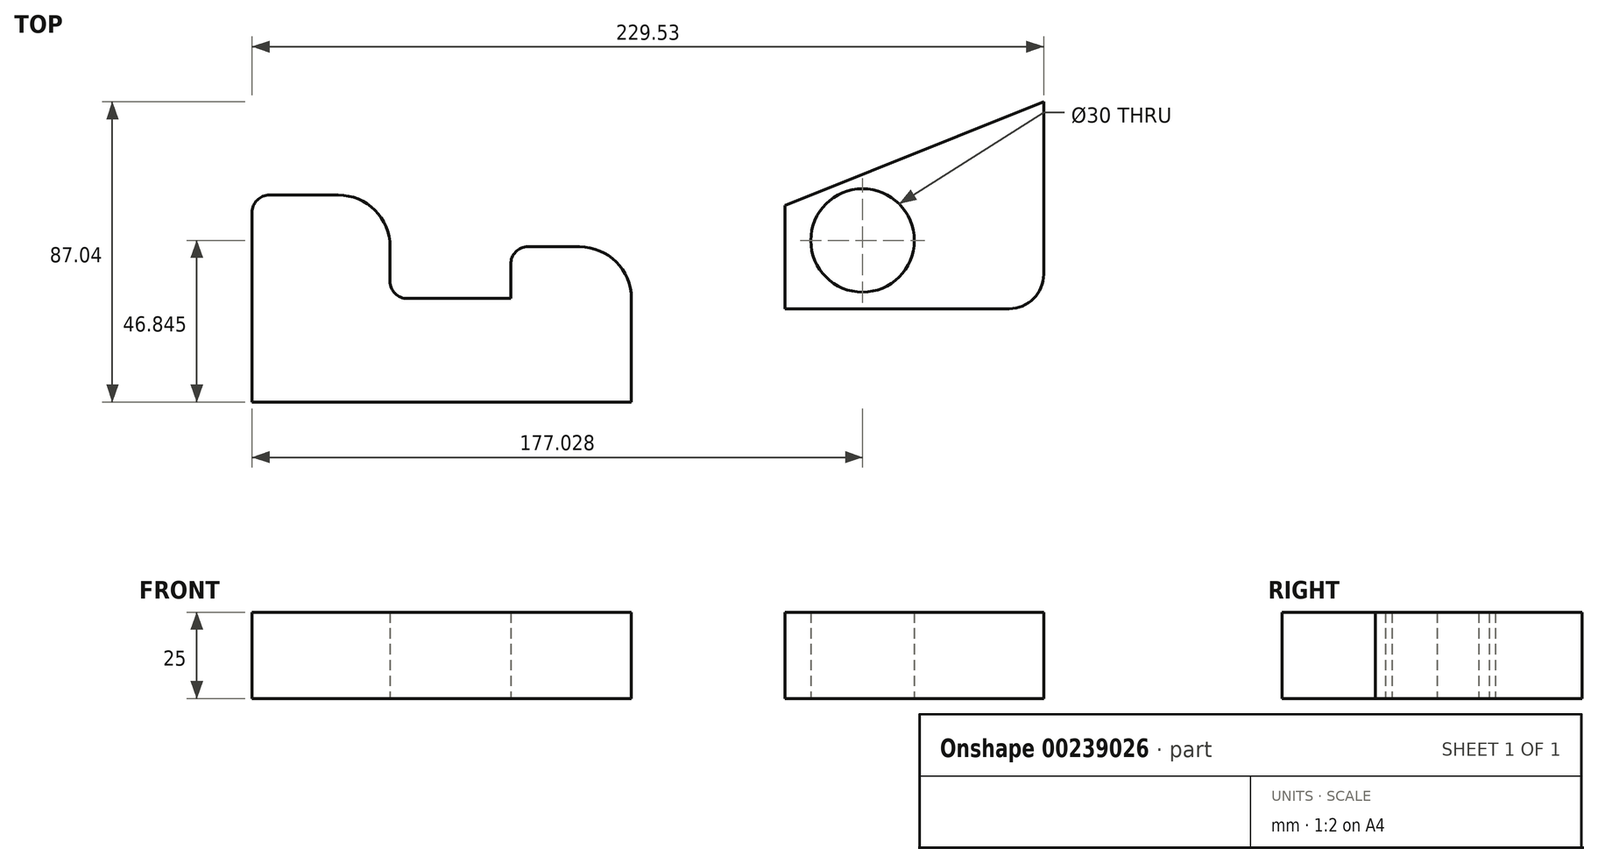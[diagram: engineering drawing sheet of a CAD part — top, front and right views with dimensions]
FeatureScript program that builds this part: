
annotation { "Feature Type Name" : "Feature", "Feature Type Description" : "" }
export const myFeature = defineFeature(function(context is Context, id is Id, definition is map)
    precondition{}
    {
        {
            var Q0;
            Q0=qCreatedBy(makeId("Top.planeOp"),FACE);
            var sketch = newSketch(context, id + "F0", { "sketchPlane" : qUnion([Q0])});
            skLineSegment(sketch, "E0", {"start": v(-99.18, -45) * mm, "end": v(10.82, -45) * mm});
            skLineSegment(sketch, "E1", {"start": v(-99.18, -45) * mm, "end": v(-99.18, 10) * mm});
            skLineSegment(sketch, "E2", {"start": v(-94.18, 15) * mm, "end": v(-74.18, 15) * mm});
            skPoint(sketch, "E3.visualSharp", {"position": v(-99.18, 15) * mm});
            skArc(sketch, "E3.filletArc", {"start": v(-94.18, 15) * mm, "mid": v(-97.72, 13.54) * mm, "end": v(-99.18, 10) * mm});
            skLineSegment(sketch, "E4", {"start": v(-59.18, 0) * mm, "end": v(-59.18, -10) * mm});
            skPoint(sketch, "E5.visualSharp", {"position": v(-59.18, 15) * mm});
            skArc(sketch, "E5.filletArc", {"start": v(-59.18, 0) * mm, "mid": v(-63.57, 10.6) * mm, "end": v(-74.18, 15) * mm});
            skLineSegment(sketch, "E6", {"start": v(-54.18, -15) * mm, "end": v(-24.18, -15) * mm});
            skPoint(sketch, "E7.visualSharp", {"position": v(-59.18, -15) * mm});
            skArc(sketch, "E7.filletArc", {"start": v(-59.18, -10) * mm, "mid": v(-57.72, -13.54) * mm, "end": v(-54.18, -15) * mm});
            skLineSegment(sketch, "E8", {"start": v(-24.18, -15) * mm, "end": v(-24.18, -5) * mm});
            skLineSegment(sketch, "E9", {"start": v(-19.18, 0) * mm, "end": v(-4.18, 0) * mm});
            skPoint(sketch, "E10.visualSharp", {"position": v(-24.18, 0) * mm});
            skArc(sketch, "E10.filletArc", {"start": v(-19.18, 0) * mm, "mid": v(-22.72, -1.46) * mm, "end": v(-24.18, -5) * mm});
            skLineSegment(sketch, "E11", {"start": v(10.82, -15) * mm, "end": v(10.82, -45) * mm});
            skLineSegment(sketch, "E12", {"start": v(10.82, -45) * mm, "end": v(10.82, -27.29) * mm});
            skPoint(sketch, "E13.visualSharp", {"position": v(10.82, 0) * mm});
            skArc(sketch, "E13.filletArc", {"start": v(10.82, -15) * mm, "mid": v(6.43, -4.4) * mm, "end": v(-4.18, 0) * mm});
            skLineSegment(sketch, "E14", {"start": v(55.35, -17.96) * mm, "end": v(120.35, -17.96) * mm});
            skLineSegment(sketch, "E15", {"start": v(130.35, -7.96) * mm, "end": v(130.35, 42.04) * mm});
            skLineSegment(sketch, "E16", {"start": v(55.35, -17.96) * mm, "end": v(55.35, 12.04) * mm});
            skLineSegment(sketch, "E17", {"start": v(55.35, 12.04) * mm, "end": v(130.35, 42.04) * mm});
            skPoint(sketch, "E18.visualSharp", {"position": v(130.35, -17.96) * mm});
            skArc(sketch, "E18.filletArc", {"start": v(120.35, -17.96) * mm, "mid": v(127.42, -15.04) * mm, "end": v(130.35, -7.96) * mm});
            skLineSegment(sketch, "E19", {"start": v(55.35, -17.96) * mm, "end": v(77.85, -17.96) * mm});
            skLineSegment(sketch, "E20", {"start": v(55.35, 12.04) * mm, "end": v(55.35, 1.84) * mm});
            skLineSegment(sketch, "E21", {"start": v(55.35, 1.84) * mm, "end": v(77.85, 1.84) * mm});
            skCircle(sketch, "E22", {"center": v(77.85, 1.84) * mm, "radius": 15 * mm});
            skSolve(sketch);
        }
        {
            var Q0;
            Q0 = qSketchRegion(id + "F0", true);
            extrude(context, id + "F1", {"entities" : qUnion([Q0]), "depth" : 25 * mm});
        }
    });
